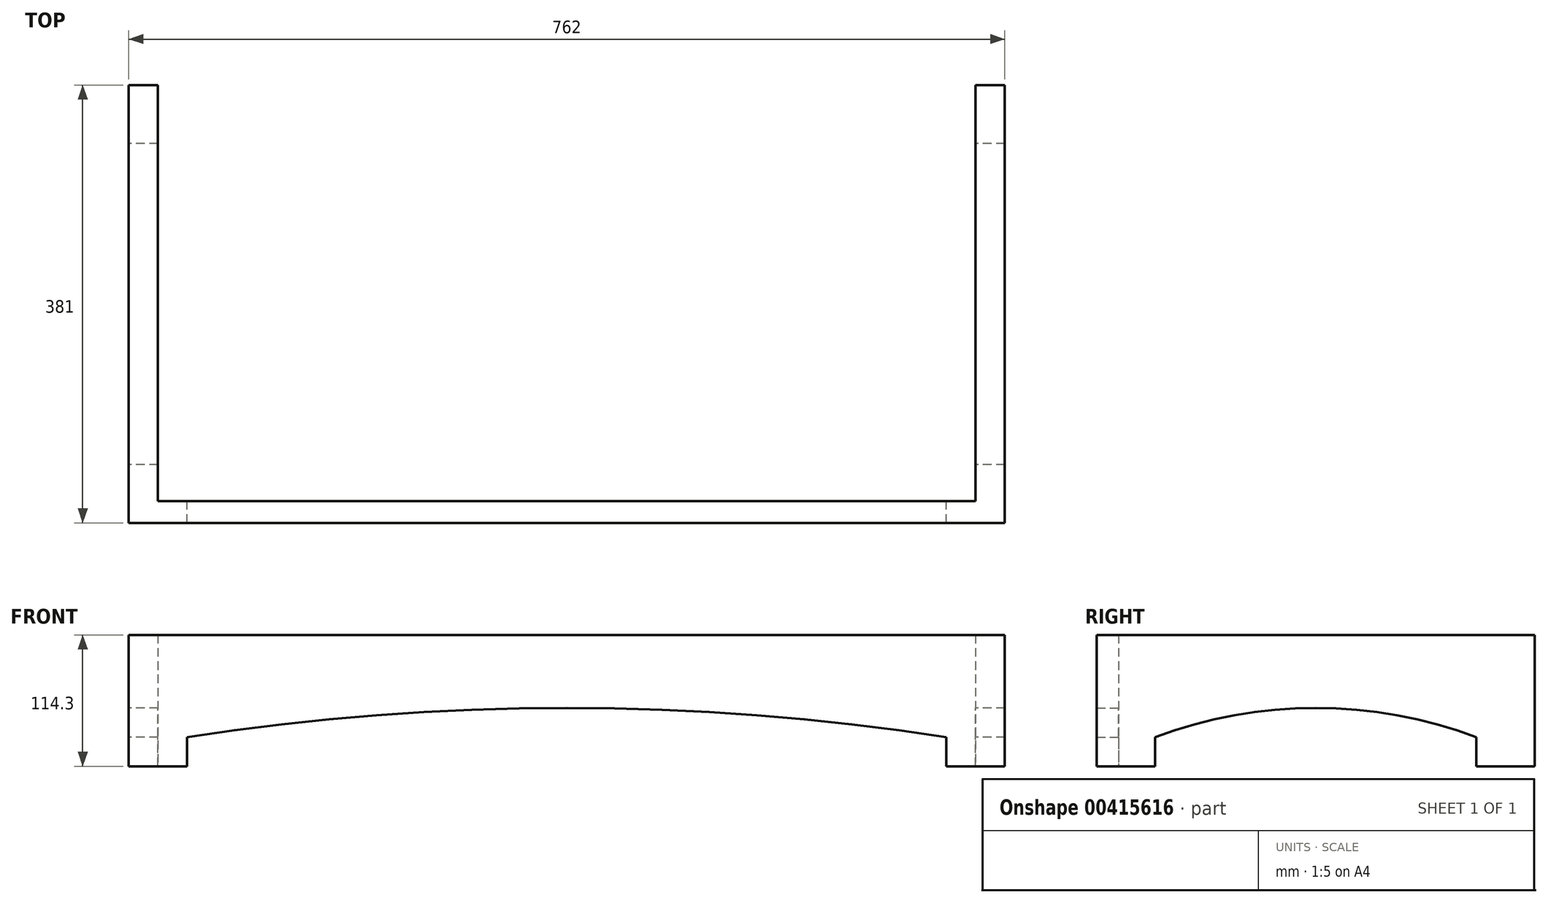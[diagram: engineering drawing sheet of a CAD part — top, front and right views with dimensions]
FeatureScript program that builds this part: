
annotation { "Feature Type Name" : "Feature", "Feature Type Description" : "" }
export const myFeature = defineFeature(function(context is Context, id is Id, definition is map)
    precondition{}
    {
        {
            var Q0;
            Q0=qCreatedBy(makeId("Front.planeOp"),FACE);
            var sketch = newSketch(context, id + "F0", { "sketchPlane" : qUnion([Q0])});
            skLineSegment(sketch, "E0.bottom", {"start": v(-381, 0) * mm, "end": v(381, 0) * mm});
            skLineSegment(sketch, "E0.top", {"start": v(-381, -114.3) * mm, "end": v(-330.2, -114.3) * mm});
            skLineSegment(sketch, "E0.left", {"start": v(-381, 0) * mm, "end": v(-381, -114.3) * mm});
            skLineSegment(sketch, "E0.right", {"start": v(381, 0) * mm, "end": v(381, -114.3) * mm});
            skLineSegment(sketch, "E1", {"start": v(-330.2, -114.3) * mm, "end": v(-330.2, -88.9) * mm});
            skArc(sketch, "E2", {"start": v(330.2, -88.9) * mm, "mid": v(0, -63.5) * mm, "end": v(-330.2, -88.9) * mm});
            skLineSegment(sketch, "E3", {"start": v(330.2, -88.9) * mm, "end": v(330.2, -114.3) * mm});
            skLineSegment(sketch, "E4.trimOffspring", {"start": v(330.2, -114.3) * mm, "end": v(381, -114.3) * mm});
            skSolve(sketch);
        }
        {
            var Q0;
            Q0=makeQuery(id+"F0.imprint","IMPRINT",FACE,{"disambiguationData":[TD([[makeQuery(id+"F0.imprint","IMPRINT",EDGE,{"derivedFrom":sQuery(id+"F0.wireOp",EDGE,"E0.bottom")}),-1.0]])]});
            extrude(context, id + "F1", {"entities" : qUnion([Q0]), "depth" : 19.05 * mm});
        }
        {
            var Q0;
            Q0=makeQuery(id+"F1.opExtrude","CAP_FACE",FACE,{"disambiguationData":[OSD([sQuery(id+"F0.wireOp",EDGE,"E0.bottom"),sQuery(id+"F0.wireOp",EDGE,"E0.top"),sQuery(id+"F0.wireOp",EDGE,"E0.left"),sQuery(id+"F0.wireOp",EDGE,"E0.right"),sQuery(id+"F0.wireOp",EDGE,"E1"),sQuery(id+"F0.wireOp",EDGE,"E2"),sQuery(id+"F0.wireOp",EDGE,"E3"),sQuery(id+"F0.wireOp",EDGE,"E4.trimOffspring")])],"isStart":true});
            var sketch = newSketch(context, id + "F2", { "sketchPlane" : qUnion([Q0])});
            skLineSegment(sketch, "E5.bottom", {"start": v(-381, 0) * mm, "end": v(-355.6, 0) * mm});
            skLineSegment(sketch, "E5.top", {"start": v(-381, -114.3) * mm, "end": v(-355.6, -114.3) * mm});
            skLineSegment(sketch, "E5.left", {"start": v(-381, 0) * mm, "end": v(-381, -114.3) * mm});
            skLineSegment(sketch, "E5.right", {"start": v(-355.6, 0) * mm, "end": v(-355.6, -114.3) * mm});
            skLineSegment(sketch, "E6.bottom", {"start": v(381, 0) * mm, "end": v(355.6, 0) * mm});
            skLineSegment(sketch, "E6.top", {"start": v(381, -114.3) * mm, "end": v(355.6, -114.3) * mm});
            skLineSegment(sketch, "E6.left", {"start": v(381, 0) * mm, "end": v(381, -114.3) * mm});
            skLineSegment(sketch, "E6.right", {"start": v(355.6, 0) * mm, "end": v(355.6, -114.3) * mm});
            skSolve(sketch);
        }
        {
            var Q0;
            Q0=makeQuery(id+"F2.imprint","IMPRINT",FACE,{"disambiguationData":[TD([[makeQuery(id+"F2.imprint","IMPRINT",EDGE,{"derivedFrom":sQuery(id+"F2.wireOp",EDGE,"E5.bottom")}),1.0]])]});
            var Q1;
            Q1=makeQuery(id+"F2.imprint","IMPRINT",FACE,{"disambiguationData":[TD([[makeQuery(id+"F2.imprint","IMPRINT",EDGE,{"derivedFrom":sQuery(id+"F2.wireOp",EDGE,"E6.bottom")}),1.0]])]});
            extrude(context, id + "F3", {"entities" : qUnion([Q0, Q1]), "operationType" : NewBodyOperationType.ADD, "depth" : 361.95 * mm});
        }
        {
            var Q0;
            Q0=makeQuery(id+"F3.boolean.opBoolean","MERGE",FACE,{"derivedFrom":[makeQuery(id+"F1.opExtrude","SWEPT_FACE",FACE,{"disambiguationData":[OSD([sQuery(id+"F0.wireOp",EDGE,"E0.left")])]}),makeQuery(id+"F3.opExtrude","SWEPT_FACE",FACE,{"disambiguationData":[OSD([sQuery(id+"F2.wireOp",EDGE,"E6.left")])]})]});
            var sketch = newSketch(context, id + "F4", { "sketchPlane" : qUnion([Q0])});
            skLineSegment(sketch, "E7", {"start": v(-311.15, -114.3) * mm, "end": v(-311.15, -88.9) * mm});
            skLineSegment(sketch, "E8", {"start": v(-31.75, -114.3) * mm, "end": v(-31.75, -88.9) * mm});
            skArc(sketch, "E9", {"start": v(-31.75, -88.9) * mm, "mid": v(-171.45, -63.5) * mm, "end": v(-311.15, -88.9) * mm});
            skLineSegment(sketch, "E10", {"start": v(-311.15, -114.3) * mm, "end": v(-31.75, -114.3) * mm});
            skSolve(sketch);
        }
        {
            var Q0;
            Q0=makeQuery(id+"F4.imprint","IMPRINT",FACE,{"disambiguationData":[TD([[makeQuery(id+"F4.imprint","IMPRINT",EDGE,{"derivedFrom":sQuery(id+"F4.wireOp",EDGE,"E7")}),-1.0]])]});
            extrude(context, id + "F5", {"entities" : qUnion([Q0]), "operationType" : NewBodyOperationType.REMOVE, "oppositeDirection" : true, "depth" : 762 * mm});
        }
    });
